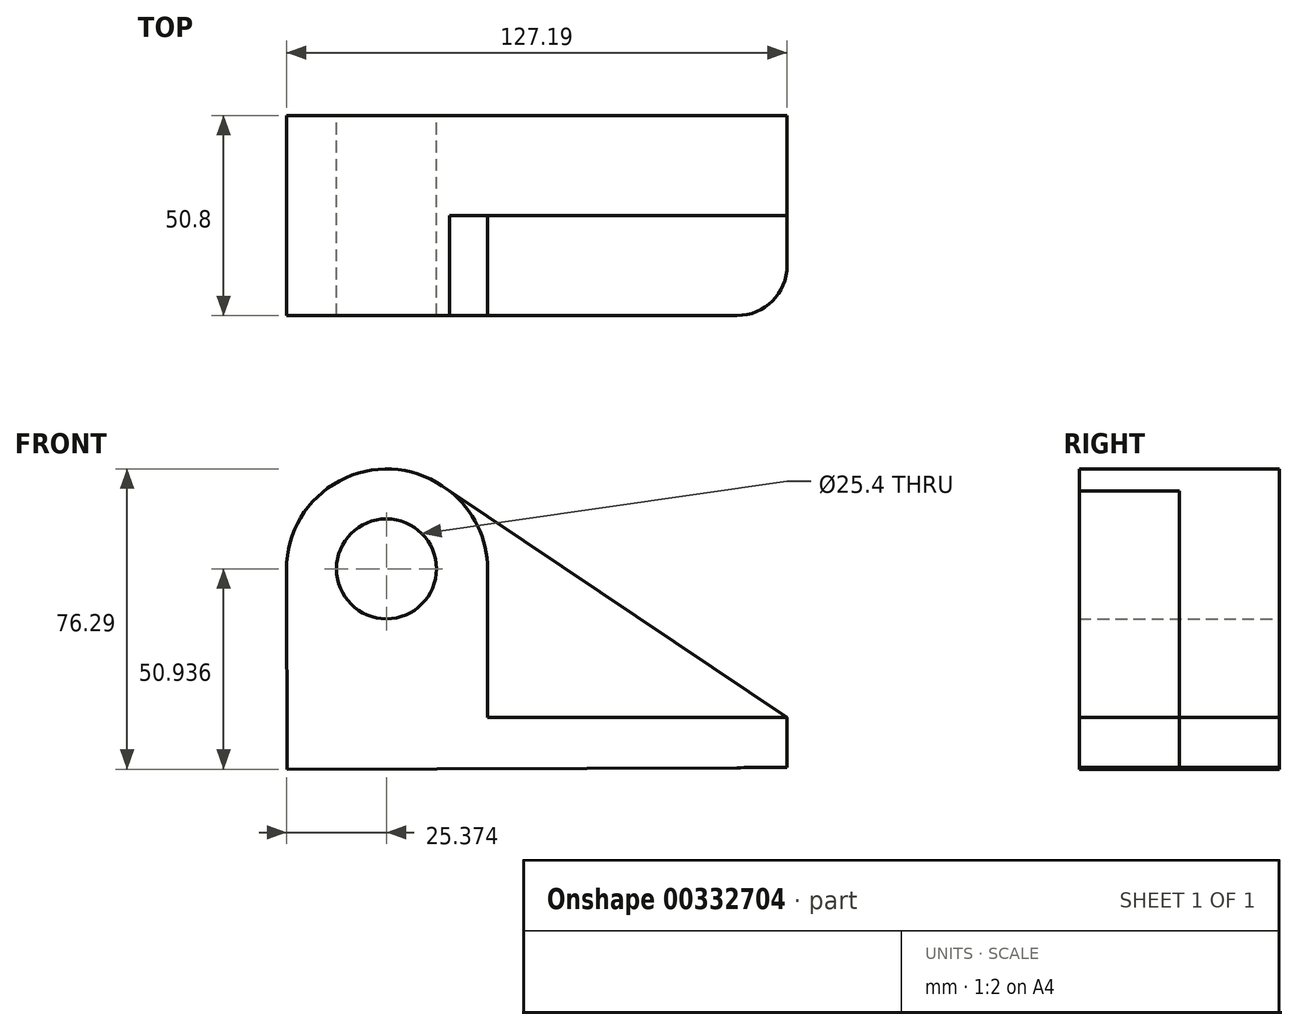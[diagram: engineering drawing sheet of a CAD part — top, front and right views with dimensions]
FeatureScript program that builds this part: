
annotation { "Feature Type Name" : "Feature", "Feature Type Description" : "" }
export const myFeature = defineFeature(function(context is Context, id is Id, definition is map)
    precondition{}
    {
        {
            var Q0;
            Q0=qCreatedBy(makeId("Front.planeOp"),FACE);
            var sketch = newSketch(context, id + "F0", { "sketchPlane" : qUnion([Q0])});
            skCircle(sketch, "E0", {"center": v(-0.3, 0.14) * mm, "radius": 12.7 * mm});
            skArc(sketch, "E1", {"start": v(13.89, 21.18) * mm, "mid": v(-12.26, 22.49) * mm, "end": v(-25.68, 0) * mm});
            skLineSegment(sketch, "E2", {"start": v(-25.68, 0) * mm, "end": v(-25.49, -50.8) * mm});
            skLineSegment(sketch, "E3", {"start": v(-25.49, -50.8) * mm, "end": v(101.5, -50.33) * mm});
            skLineSegment(sketch, "E4", {"start": v(101.5, -50.33) * mm, "end": v(101.46, -37.63) * mm});
            skLineSegment(sketch, "E5", {"start": v(101.46, -37.63) * mm, "end": v(13.89, 21.18) * mm});
            skSolve(sketch);
        }
        {
            var Q0;
            Q0=makeQuery(id+"F0.imprint","IMPRINT",FACE,{"disambiguationData":[TD([[makeQuery(id+"F0.imprint","IMPRINT",EDGE,{"derivedFrom":sQuery(id+"F0.wireOp",EDGE,"E0")}),-1.0]])]});
            extrude(context, id + "F1", {"entities" : qUnion([Q0]), "depth" : 25.4 * mm});
        }
        {
            var Q0;
            Q0=makeQuery(id+"F1.opExtrude","CAP_FACE",FACE,{"disambiguationData":[OSD([sQuery(id+"F0.wireOp",EDGE,"E0"),sQuery(id+"F0.wireOp",EDGE,"E1"),sQuery(id+"F0.wireOp",EDGE,"E2"),sQuery(id+"F0.wireOp",EDGE,"E3"),sQuery(id+"F0.wireOp",EDGE,"E4"),sQuery(id+"F0.wireOp",EDGE,"E5")])],"isStart":false});
            var sketch = newSketch(context, id + "F2", { "sketchPlane" : qUnion([Q0])});
            skArc(sketch, "E6", {"start": v(25.4, 0) * mm, "mid": v(0, 25.4) * mm, "end": v(-25.4, 0) * mm});
            skLineSegment(sketch, "E7", {"start": v(25.4, 0) * mm, "end": v(25.4, -37.63) * mm});
            skLineSegment(sketch, "E8", {"start": v(-25.68, 0) * mm, "end": v(-25.54, -38.1) * mm});
            skLineSegment(sketch, "E9.bottom", {"start": v(101.46, -37.63) * mm, "end": v(25.4, -37.63) * mm});
            skLineSegment(sketch, "E9.top", {"start": v(101.46, -50.8) * mm, "end": v(-25.49, -50.8) * mm});
            skLineSegment(sketch, "E9.left", {"start": v(101.46, -37.63) * mm, "end": v(101.46, -50.8) * mm});
            skLineSegment(sketch, "E9.right", {"start": v(-25.49, -37.63) * mm, "end": v(-25.49, -50.8) * mm});
            skSolve(sketch);
        }
        {
            var Q0;
            {var subQ12=sQuery(id+"F2.wireOp",EDGE,"E7");Q0=makeQuery(id+"F2.imprint","IMPRINT",FACE,{"disambiguationData":[TD([[makeQuery(id+"F2.imprint","IMPRINT",EDGE,{"derivedFrom":subQ12}),-1.0]])]});}
            extrude(context, id + "F3", {"entities" : qUnion([Q0]), "operationType" : NewBodyOperationType.ADD, "depth" : 25.4 * mm});
        }
        {
            var Q0;
            {var subQ12=sQuery(id+"F2.wireOp",EDGE,"E7");Q0=makeQuery(id+"F2.imprint","IMPRINT",FACE,{"disambiguationData":[TD([[makeQuery(id+"F2.imprint","IMPRINT",EDGE,{"derivedFrom":subQ12}),-1.0]])]});}
            extrude(context, id + "F4", {"entities" : qUnion([Q0]), "operationType" : NewBodyOperationType.ADD, "depth" : 25.4 * mm});
        }
        {
            var Q0;
            Q0=makeQuery(id+"F3.opExtrude","CAP_EDGE",EDGE,{"disambiguationData":[OSD([sQuery(id+"F2.wireOp",EDGE,"E9.left")])],"isStart":false});
            fillet(context, id + "F5", {"entities" : qUnion([Q0]), "radius" : 12.7 * mm, "tangentPropagation" : true, "allowEdgeOverflow" : false});
        }
    });
